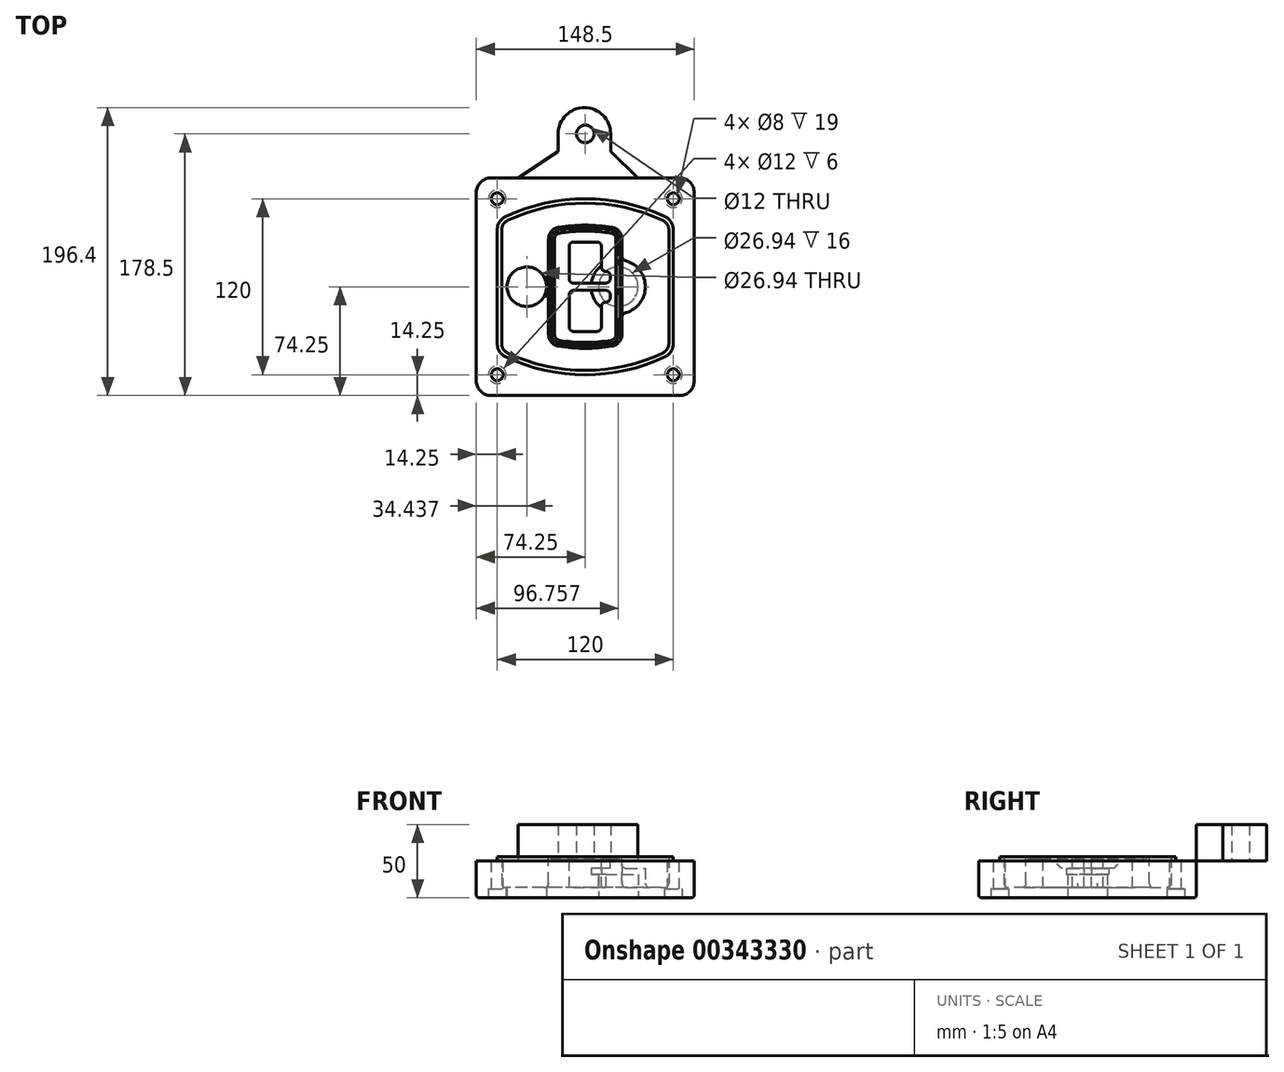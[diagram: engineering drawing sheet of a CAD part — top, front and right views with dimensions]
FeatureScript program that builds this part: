
annotation { "Feature Type Name" : "Feature", "Feature Type Description" : "" }
export const myFeature = defineFeature(function(context is Context, id is Id, definition is map)
    precondition{}
    {
        {
            var Q0;
            Q0=qCreatedBy(makeId("Top.planeOp"),FACE);
            var sketch = newSketch(context, id + "F0", { "sketchPlane" : qUnion([Q0])});
            skPoint(sketch, "E0.rect.middle", {"position": v(0, 0) * mm});
            skLineSegment(sketch, "E1.bottom", {"start": v(-64.25, -74.25) * mm, "end": v(64.25, -74.25) * mm});
            skLineSegment(sketch, "E1.top", {"start": v(-64.25, 74.25) * mm, "end": v(64.25, 74.25) * mm});
            skLineSegment(sketch, "E1.left", {"start": v(-74.25, -64.25) * mm, "end": v(-74.25, 64.25) * mm});
            skLineSegment(sketch, "E1.right", {"start": v(74.25, -64.25) * mm, "end": v(74.25, 64.25) * mm});
            skLineSegment(sketch, "E2", {"start": v(-74.25, 74.25) * mm, "end": v(74.25, -74.25) * mm, "construction": true});
            skLineSegment(sketch, "E3", {"start": v(74.25, 74.25) * mm, "end": v(-74.25, -74.25) * mm, "construction": true});
            skCircle(sketch, "E4", {"center": v(-60, 60) * mm, "radius": 4 * mm});
            skCircle(sketch, "E5", {"center": v(60, 60) * mm, "radius": 4 * mm});
            skCircle(sketch, "E6", {"center": v(60, -60) * mm, "radius": 4 * mm});
            skCircle(sketch, "E7", {"center": v(-60, -60) * mm, "radius": 4 * mm});
            skLineSegment(sketch, "E8", {"start": v(-60, 60) * mm, "end": v(60, 60) * mm, "construction": true});
            skLineSegment(sketch, "E9", {"start": v(60, 60) * mm, "end": v(60, -60) * mm, "construction": true});
            skLineSegment(sketch, "E10", {"start": v(60, -60) * mm, "end": v(-60, -60) * mm, "construction": true});
            skLineSegment(sketch, "E11", {"start": v(-60, -60) * mm, "end": v(-60, 60) * mm, "construction": true});
            skLineSegment(sketch, "E12", {"start": v(-60, 38.83) * mm, "end": v(-60, -38.83) * mm});
            skLineSegment(sketch, "E13", {"start": v(60, 38.83) * mm, "end": v(60, -38.83) * mm});
            skArc(sketch, "E14", {"start": v(54.26, 47.88) * mm, "mid": v(0, 60) * mm, "end": v(-54.26, 47.88) * mm});
            skArc(sketch, "E15", {"start": v(-54.26, -47.88) * mm, "mid": v(0, -60) * mm, "end": v(54.26, -47.88) * mm});
            skLineSegment(sketch, "E16", {"start": v(-60, 0) * mm, "end": v(60, 0) * mm, "construction": true});
            skPoint(sketch, "E17.visualSharp", {"position": v(-60, -45) * mm});
            skArc(sketch, "E17.filletArc", {"start": v(-60, -38.83) * mm, "mid": v(-58.44, -44.2) * mm, "end": v(-54.26, -47.88) * mm});
            skPoint(sketch, "E18.visualSharp", {"position": v(-60, 45) * mm});
            skArc(sketch, "E18.filletArc", {"start": v(-54.26, 47.88) * mm, "mid": v(-58.44, 44.2) * mm, "end": v(-60, 38.83) * mm});
            skPoint(sketch, "E19.visualSharp", {"position": v(60, 45) * mm});
            skArc(sketch, "E19.filletArc", {"start": v(60, 38.83) * mm, "mid": v(58.44, 44.2) * mm, "end": v(54.26, 47.88) * mm});
            skPoint(sketch, "E20.visualSharp", {"position": v(60, -45) * mm});
            skArc(sketch, "E20.filletArc", {"start": v(54.26, -47.88) * mm, "mid": v(58.44, -44.2) * mm, "end": v(60, -38.83) * mm});
            skPoint(sketch, "E21.visualSharp", {"position": v(-74.25, 74.25) * mm});
            skArc(sketch, "E21.filletArc", {"start": v(-64.25, 74.25) * mm, "mid": v(-71.32, 71.32) * mm, "end": v(-74.25, 64.25) * mm});
            skPoint(sketch, "E22.visualSharp", {"position": v(74.25, 74.25) * mm});
            skArc(sketch, "E22.filletArc", {"start": v(74.25, 64.25) * mm, "mid": v(71.32, 71.32) * mm, "end": v(64.25, 74.25) * mm});
            skPoint(sketch, "E23.visualSharp", {"position": v(74.25, -74.25) * mm});
            skArc(sketch, "E23.filletArc", {"start": v(64.25, -74.25) * mm, "mid": v(71.32, -71.32) * mm, "end": v(74.25, -64.25) * mm});
            skPoint(sketch, "E24.visualSharp", {"position": v(-74.25, -74.25) * mm});
            skArc(sketch, "E24.filletArc", {"start": v(-74.25, -64.25) * mm, "mid": v(-71.32, -71.32) * mm, "end": v(-64.25, -74.25) * mm});
            skArc(sketch, "E25.0", {"start": v(57, 38.83) * mm, "mid": v(55.9, 42.58) * mm, "end": v(52.98, 45.17) * mm});
            skLineSegment(sketch, "E25.1", {"start": v(57, 38.83) * mm, "end": v(57, -38.83) * mm});
            skArc(sketch, "E25.2", {"start": v(52.98, -45.17) * mm, "mid": v(55.9, -42.58) * mm, "end": v(57, -38.83) * mm});
            skArc(sketch, "E25.3", {"start": v(-52.98, -45.17) * mm, "mid": v(0, -57) * mm, "end": v(52.98, -45.17) * mm});
            skArc(sketch, "E25.4", {"start": v(-57, -38.83) * mm, "mid": v(-55.9, -42.58) * mm, "end": v(-52.98, -45.17) * mm});
            skArc(sketch, "E25.5", {"start": v(52.98, 45.17) * mm, "mid": v(0, 57) * mm, "end": v(-52.98, 45.17) * mm});
            skLineSegment(sketch, "E25.6", {"start": v(-57, 38.83) * mm, "end": v(-57, -38.83) * mm});
            skArc(sketch, "E25.7", {"start": v(-52.98, 45.17) * mm, "mid": v(-55.9, 42.58) * mm, "end": v(-57, 38.83) * mm});
            skArc(sketch, "E26.0", {"start": v(-55.96, 51.5) * mm, "mid": v(-61.82, 46.33) * mm, "end": v(-64, 38.83) * mm});
            skArc(sketch, "E26.1", {"start": v(55.96, 51.5) * mm, "mid": v(0, 64) * mm, "end": v(-55.96, 51.5) * mm});
            skArc(sketch, "E26.2", {"start": v(64, 38.83) * mm, "mid": v(61.82, 46.33) * mm, "end": v(55.96, 51.5) * mm});
            skLineSegment(sketch, "E26.3", {"start": v(64, 38.83) * mm, "end": v(64, -38.83) * mm});
            skArc(sketch, "E26.4", {"start": v(55.96, -51.5) * mm, "mid": v(61.82, -46.33) * mm, "end": v(64, -38.83) * mm});
            skLineSegment(sketch, "E26.5", {"start": v(-64, 38.83) * mm, "end": v(-64, -38.83) * mm});
            skArc(sketch, "E26.6", {"start": v(-55.96, -51.5) * mm, "mid": v(0, -64) * mm, "end": v(55.96, -51.5) * mm});
            skArc(sketch, "E26.7", {"start": v(-64, -38.83) * mm, "mid": v(-61.82, -46.33) * mm, "end": v(-55.96, -51.5) * mm});
            skSolve(sketch);
        }
        {
            var Q0;
            Q0=makeQuery(id+"F0.imprint","IMPRINT",FACE,{"disambiguationData":[TD([[makeQuery(id+"F0.imprint","IMPRINT",EDGE,{"derivedFrom":sQuery(id+"F0.wireOp",EDGE,"E1.bottom")}),1.0]])]});
            var Q1;
            Q1=makeQuery(id+"F0.imprint","IMPRINT",FACE,{"disambiguationData":[TD([[makeQuery(id+"F0.imprint","IMPRINT",EDGE,{"derivedFrom":sQuery(id+"F0.wireOp",EDGE,"E12")}),1.0]])]});
            var Q2;
            Q2=makeQuery(id+"F0.imprint","IMPRINT",FACE,{"disambiguationData":[TD([[makeQuery(id+"F0.imprint","IMPRINT",EDGE,{"derivedFrom":sQuery(id+"F0.wireOp",EDGE,"E25.0")}),1.0]])]});
            var Q3;
            Q3=makeQuery(id+"F0.imprint","IMPRINT",FACE,{"disambiguationData":[TD([[makeQuery(id+"F0.imprint","IMPRINT",EDGE,{"derivedFrom":sQuery(id+"F0.wireOp",EDGE,"E12")}),-1.0]])]});
            extrude(context, id + "F1", {"entities" : qUnion([Q0, Q1, Q2, Q3]), "oppositeDirection" : true, "depth" : 25 * mm});
        }
        {
            var Q0;
            Q0=makeQuery(id+"F0.imprint","IMPRINT",FACE,{"disambiguationData":[TD([[makeQuery(id+"F0.imprint","IMPRINT",EDGE,{"derivedFrom":sQuery(id+"F0.wireOp",EDGE,"E12")}),1.0]])]});
            extrude(context, id + "F2", {"entities" : qUnion([Q0]), "operationType" : NewBodyOperationType.ADD, "depth" : 3 * mm});
        }
        {
            var Q0;
            Q0=makeQuery(id+"F0.imprint","IMPRINT",FACE,{"disambiguationData":[TD([[makeQuery(id+"F0.imprint","IMPRINT",EDGE,{"derivedFrom":sQuery(id+"F0.wireOp",EDGE,"E25.0")}),1.0]])]});
            extrude(context, id + "F3", {"entities" : qUnion([Q0]), "operationType" : NewBodyOperationType.REMOVE, "oppositeDirection" : true, "depth" : 18 * mm});
        }
        {
            var Q0;
            Q0=makeQuery(id+"F2.opExtrude","CAP_FACE",FACE,{"disambiguationData":[OSD([sQuery(id+"F0.wireOp",EDGE,"E12"),sQuery(id+"F0.wireOp",EDGE,"E13"),sQuery(id+"F0.wireOp",EDGE,"E14"),sQuery(id+"F0.wireOp",EDGE,"E15"),sQuery(id+"F0.wireOp",EDGE,"E17.filletArc"),sQuery(id+"F0.wireOp",EDGE,"E18.filletArc"),sQuery(id+"F0.wireOp",EDGE,"E19.filletArc"),sQuery(id+"F0.wireOp",EDGE,"E20.filletArc"),sQuery(id+"F0.wireOp",EDGE,"E25.0"),sQuery(id+"F0.wireOp",EDGE,"E25.1"),sQuery(id+"F0.wireOp",EDGE,"E25.2"),sQuery(id+"F0.wireOp",EDGE,"E25.3"),sQuery(id+"F0.wireOp",EDGE,"E25.4"),sQuery(id+"F0.wireOp",EDGE,"E25.5"),sQuery(id+"F0.wireOp",EDGE,"E25.6"),sQuery(id+"F0.wireOp",EDGE,"E25.7")])],"isStart":false});
            var sketch = newSketch(context, id + "F4", { "sketchPlane" : qUnion([Q0])});
            skArc(sketch, "E27.0", {"start": v(-18.34, -40.45) * mm, "mid": v(0, -42) * mm, "end": v(18.34, -40.45) * mm});
            skArc(sketch, "E28.0", {"start": v(18.34, 40.45) * mm, "mid": v(0, 42) * mm, "end": v(-18.34, 40.45) * mm});
            skLineSegment(sketch, "E29", {"start": v(-25, 32.57) * mm, "end": v(-25, -32.57) * mm});
            skLineSegment(sketch, "E30", {"start": v(25, 32.57) * mm, "end": v(25, -32.57) * mm});
            skLineSegment(sketch, "E31", {"start": v(-25, 39.1) * mm, "end": v(25, 39.1) * mm, "construction": true});
            skLineSegment(sketch, "E32", {"start": v(-25, -39.1) * mm, "end": v(25, -39.1) * mm, "construction": true});
            skPoint(sketch, "E33.visualSharp", {"position": v(-25, 39.1) * mm});
            skArc(sketch, "E33.filletArc", {"start": v(-18.34, 40.45) * mm, "mid": v(-23.11, 37.73) * mm, "end": v(-25, 32.57) * mm});
            skPoint(sketch, "E34.visualSharp", {"position": v(25, 39.1) * mm});
            skArc(sketch, "E34.filletArc", {"start": v(25, 32.57) * mm, "mid": v(23.11, 37.73) * mm, "end": v(18.34, 40.45) * mm});
            skPoint(sketch, "E35.visualSharp", {"position": v(25, -39.1) * mm});
            skArc(sketch, "E35.filletArc", {"start": v(18.34, -40.45) * mm, "mid": v(23.11, -37.73) * mm, "end": v(25, -32.57) * mm});
            skPoint(sketch, "E36.visualSharp", {"position": v(-25, -39.1) * mm});
            skArc(sketch, "E36.filletArc", {"start": v(-25, -32.57) * mm, "mid": v(-23.11, -37.73) * mm, "end": v(-18.34, -40.45) * mm});
            skArc(sketch, "E37.0", {"start": v(52.98, 45.17) * mm, "mid": v(0, 57) * mm, "end": v(-52.98, 45.17) * mm});
            skArc(sketch, "E37.1", {"start": v(-52.98, 45.17) * mm, "mid": v(-55.9, 42.58) * mm, "end": v(-57, 38.83) * mm});
            skLineSegment(sketch, "E37.2", {"start": v(-57, 38.83) * mm, "end": v(-57, -38.83) * mm});
            skArc(sketch, "E37.3", {"start": v(-57, -38.83) * mm, "mid": v(-55.9, -42.58) * mm, "end": v(-52.98, -45.17) * mm});
            skArc(sketch, "E37.4", {"start": v(-52.98, -45.17) * mm, "mid": v(0, -57) * mm, "end": v(52.98, -45.17) * mm});
            skArc(sketch, "E37.5", {"start": v(52.98, -45.17) * mm, "mid": v(55.9, -42.58) * mm, "end": v(57, -38.83) * mm});
            skLineSegment(sketch, "E37.6", {"start": v(57, 38.83) * mm, "end": v(57, -38.83) * mm});
            skArc(sketch, "E37.7", {"start": v(57, 38.83) * mm, "mid": v(55.9, 42.58) * mm, "end": v(52.98, 45.17) * mm});
            skLineSegment(sketch, "E38.0", {"start": v(23, 32.57) * mm, "end": v(23, -32.57) * mm});
            skArc(sketch, "E38.1", {"start": v(18, -38.48) * mm, "mid": v(21.58, -36.44) * mm, "end": v(23, -32.57) * mm});
            skArc(sketch, "E38.2", {"start": v(-18, -38.48) * mm, "mid": v(0, -40) * mm, "end": v(18, -38.48) * mm});
            skArc(sketch, "E38.3", {"start": v(-23, -32.57) * mm, "mid": v(-21.58, -36.44) * mm, "end": v(-18, -38.48) * mm});
            skLineSegment(sketch, "E38.4", {"start": v(-23, 32.57) * mm, "end": v(-23, -32.57) * mm});
            skArc(sketch, "E38.5", {"start": v(23, 32.57) * mm, "mid": v(21.58, 36.44) * mm, "end": v(18, 38.48) * mm});
            skArc(sketch, "E38.6", {"start": v(-18, 38.48) * mm, "mid": v(-21.58, 36.44) * mm, "end": v(-23, 32.57) * mm});
            skArc(sketch, "E38.7", {"start": v(18, 38.48) * mm, "mid": v(0, 40) * mm, "end": v(-18, 38.48) * mm});
            skArc(sketch, "E39.0", {"start": v(21, 32.57) * mm, "mid": v(20.06, 35.15) * mm, "end": v(17.67, 36.5) * mm});
            skLineSegment(sketch, "E39.1", {"start": v(21, 32.57) * mm, "end": v(21, -32.57) * mm});
            skArc(sketch, "E39.2", {"start": v(17.67, -36.5) * mm, "mid": v(20.06, -35.15) * mm, "end": v(21, -32.57) * mm});
            skArc(sketch, "E39.3", {"start": v(-17.67, -36.5) * mm, "mid": v(0, -38) * mm, "end": v(17.67, -36.5) * mm});
            skArc(sketch, "E39.4", {"start": v(-21, -32.57) * mm, "mid": v(-20.06, -35.15) * mm, "end": v(-17.67, -36.5) * mm});
            skArc(sketch, "E39.5", {"start": v(17.67, 36.5) * mm, "mid": v(0, 38) * mm, "end": v(-17.67, 36.5) * mm});
            skLineSegment(sketch, "E39.6", {"start": v(-21, 32.57) * mm, "end": v(-21, -32.57) * mm});
            skArc(sketch, "E39.7", {"start": v(-17.67, 36.5) * mm, "mid": v(-20.06, 35.15) * mm, "end": v(-21, 32.57) * mm});
            skLineSegment(sketch, "E40", {"start": v(-25, 0) * mm, "end": v(25, 0) * mm, "construction": true});
            skLineSegment(sketch, "E41", {"start": v(-11, 5.5) * mm, "end": v(-11, 27.5) * mm});
            skLineSegment(sketch, "E42", {"start": v(-8, 30.5) * mm, "end": v(8, 30.5) * mm});
            skLineSegment(sketch, "E43", {"start": v(11, 27.5) * mm, "end": v(11, 13.5) * mm});
            skLineSegment(sketch, "E44", {"start": v(14, 10.5) * mm, "end": v(14, 10.5) * mm});
            skLineSegment(sketch, "E45", {"start": v(17, 7.5) * mm, "end": v(17, 5.5) * mm});
            skLineSegment(sketch, "E46", {"start": v(14, 2.5) * mm, "end": v(-8, 2.5) * mm});
            skPoint(sketch, "E47.visualSharp", {"position": v(-11, 30.5) * mm});
            skArc(sketch, "E47.filletArc", {"start": v(-8, 30.5) * mm, "mid": v(-10.12, 29.62) * mm, "end": v(-11, 27.5) * mm});
            skPoint(sketch, "E48.visualSharp", {"position": v(11, 30.5) * mm});
            skArc(sketch, "E48.filletArc", {"start": v(11, 27.5) * mm, "mid": v(10.12, 29.62) * mm, "end": v(8, 30.5) * mm});
            skPoint(sketch, "E49.visualSharp", {"position": v(11, 10.5) * mm});
            skArc(sketch, "E49.filletArc", {"start": v(11, 13.5) * mm, "mid": v(11.88, 11.38) * mm, "end": v(14, 10.5) * mm});
            skPoint(sketch, "E50.visualSharp", {"position": v(17, 10.5) * mm});
            skArc(sketch, "E50.filletArc", {"start": v(17, 7.5) * mm, "mid": v(16.12, 9.62) * mm, "end": v(14, 10.5) * mm});
            skPoint(sketch, "E51.visualSharp", {"position": v(17, 2.5) * mm});
            skArc(sketch, "E51.filletArc", {"start": v(14, 2.5) * mm, "mid": v(16.12, 3.38) * mm, "end": v(17, 5.5) * mm});
            skPoint(sketch, "E52.visualSharp", {"position": v(-11, 2.5) * mm});
            skArc(sketch, "E52.filletArc", {"start": v(-11, 5.5) * mm, "mid": v(-10.12, 3.38) * mm, "end": v(-8, 2.5) * mm});
            skLineSegment(sketch, "E53.0.MirrorCS", {"start": v(14, -2.5) * mm, "end": v(-8, -2.5) * mm});
            skArc(sketch, "E54.0.MirrorCS", {"start": v(-11, -5.5) * mm, "mid": v(-10.12, -3.38) * mm, "end": v(-8, -2.5) * mm});
            skLineSegment(sketch, "E55.0.MirrorCS", {"start": v(-11, -5.5) * mm, "end": v(-11, -27.5) * mm});
            skArc(sketch, "E56.0.MirrorCS", {"start": v(-8, -30.5) * mm, "mid": v(-10.12, -29.62) * mm, "end": v(-11, -27.5) * mm});
            skLineSegment(sketch, "E57.0.MirrorCS", {"start": v(-8, -30.5) * mm, "end": v(8, -30.5) * mm});
            skArc(sketch, "E58.0.MirrorCS", {"start": v(11, -27.5) * mm, "mid": v(10.12, -29.62) * mm, "end": v(8, -30.5) * mm});
            skLineSegment(sketch, "E59.0.MirrorCS", {"start": v(11, -27.5) * mm, "end": v(11, -13.5) * mm});
            skArc(sketch, "E60.0.MirrorCS", {"start": v(11, -13.5) * mm, "mid": v(11.88, -11.38) * mm, "end": v(14, -10.5) * mm});
            skArc(sketch, "E61.0.MirrorCS", {"start": v(17, -7.5) * mm, "mid": v(16.12, -9.62) * mm, "end": v(14, -10.5) * mm});
            skLineSegment(sketch, "E62.0.MirrorCS", {"start": v(17, -7.5) * mm, "end": v(17, -5.5) * mm});
            skArc(sketch, "E63.0.MirrorCS", {"start": v(14, -2.5) * mm, "mid": v(16.12, -3.38) * mm, "end": v(17, -5.5) * mm});
            skSolve(sketch);
        }
        {
            var Q0;
            Q0=makeQuery(id+"F4.imprint","IMPRINT",FACE,{"disambiguationData":[TD([[makeQuery(id+"F4.imprint","IMPRINT",EDGE,{"derivedFrom":sQuery(id+"F4.wireOp",EDGE,"E27.0")}),1.0]])]});
            var Q1;
            Q1=makeQuery(id+"F4.imprint","IMPRINT",FACE,{"disambiguationData":[TD([[makeQuery(id+"F4.imprint","IMPRINT",EDGE,{"derivedFrom":sQuery(id+"F4.wireOp",EDGE,"E38.0")}),-1.0]])]});
            var Q2;
            Q2=makeQuery(id+"F4.imprint","IMPRINT",FACE,{"disambiguationData":[TD([[makeQuery(id+"F4.imprint","IMPRINT",EDGE,{"derivedFrom":sQuery(id+"F4.wireOp",EDGE,"E39.0")}),1.0]])]});
            extrude(context, id + "F5", {"entities" : qUnion([Q0, Q1, Q2]), "operationType" : NewBodyOperationType.ADD, "endBound" : BoundingType.UP_TO_NEXT, "oppositeDirection" : true, "depth" : 25 * mm});
        }
        {
            var Q0;
            Q0=makeQuery(id+"F4.imprint","IMPRINT",FACE,{"disambiguationData":[TD([[makeQuery(id+"F4.imprint","IMPRINT",EDGE,{"derivedFrom":sQuery(id+"F4.wireOp",EDGE,"E38.0")}),-1.0]])]});
            extrude(context, id + "F6", {"entities" : qUnion([Q0]), "operationType" : NewBodyOperationType.REMOVE, "oppositeDirection" : true, "depth" : 2 * mm});
        }
        {
            var Q0;
            Q0=makeQuery(id+"F1.opExtrude","CAP_FACE",FACE,{"disambiguationData":[OSD([sQuery(id+"F0.wireOp",EDGE,"E1.bottom"),sQuery(id+"F0.wireOp",EDGE,"E1.top"),sQuery(id+"F0.wireOp",EDGE,"E1.left"),sQuery(id+"F0.wireOp",EDGE,"E1.right"),sQuery(id+"F0.wireOp",EDGE,"E4"),sQuery(id+"F0.wireOp",EDGE,"E5"),sQuery(id+"F0.wireOp",EDGE,"E6"),sQuery(id+"F0.wireOp",EDGE,"E7"),sQuery(id+"F0.wireOp",EDGE,"E21.filletArc"),sQuery(id+"F0.wireOp",EDGE,"E22.filletArc"),sQuery(id+"F0.wireOp",EDGE,"E23.filletArc"),sQuery(id+"F0.wireOp",EDGE,"E24.filletArc")])],"isStart":false});
            var sketch = newSketch(context, id + "F7", { "sketchPlane" : qUnion([Q0])});
            skCircle(sketch, "E64", {"center": v(22.5, 0) * mm, "radius": 13.47 * mm});
            skCircle(sketch, "E65", {"center": v(-39.81, 0) * mm, "radius": 13.47 * mm});
            skLineSegment(sketch, "E66", {"start": v(74.25, 0) * mm, "end": v(-74.25, 0) * mm});
            skCircle(sketch, "E67", {"center": v(22.5, 0) * mm, "radius": 18.47 * mm});
            skCircle(sketch, "E68", {"center": v(60, -60) * mm, "radius": 6 * mm});
            skCircle(sketch, "E69", {"center": v(-60, -60) * mm, "radius": 6 * mm});
            skCircle(sketch, "E70", {"center": v(-60, 60) * mm, "radius": 6 * mm});
            skCircle(sketch, "E71", {"center": v(60, 60) * mm, "radius": 6 * mm});
            skSolve(sketch);
        }
        {
            var Q0;
            {var subQ1=sQuery(id+"F7.wireOp",EDGE,"E66");var subQ4=sQuery(id+"F7.wireOp",EDGE,"E64");var subQ6=makeQuery(id+"F7.imprint","INTERSECT",VERTEX,{"disambiguationData":[OD(0.0)],"derivedFrom":[subQ4,subQ1]});Q0=makeQuery(id+"F7.imprint","IMPRINT",FACE,{"disambiguationData":[TD([[makeQuery(id+"F7.imprint","IMPRINT",EDGE,{"disambiguationData":[TD([[subQ6,-1.0]])],"derivedFrom":subQ4}),-1.0]])]});}
            var Q1;
            {var subQ0=sQuery(id+"F7.wireOp",EDGE,"E66");var subQ1=sQuery(id+"F7.wireOp",EDGE,"E64");var subQ3=makeQuery(id+"F7.imprint","INTERSECT",VERTEX,{"disambiguationData":[OD(0.0)],"derivedFrom":[subQ1,subQ0]});Q1=makeQuery(id+"F7.imprint","IMPRINT",FACE,{"disambiguationData":[TD([[makeQuery(id+"F7.imprint","IMPRINT",EDGE,{"disambiguationData":[TD([[subQ3,-1.0]])],"derivedFrom":subQ1}),1.0]])]});}
            var Q2;
            {var subQ0=sQuery(id+"F7.wireOp",EDGE,"E66");var subQ1=sQuery(id+"F7.wireOp",EDGE,"E64");var subQ3=makeQuery(id+"F7.imprint","INTERSECT",VERTEX,{"disambiguationData":[OD(0.0)],"derivedFrom":[subQ1,subQ0]});Q2=makeQuery(id+"F7.imprint","IMPRINT",FACE,{"disambiguationData":[TD([[makeQuery(id+"F7.imprint","IMPRINT",EDGE,{"disambiguationData":[TD([[subQ3,1.0]])],"derivedFrom":subQ1}),1.0]])]});}
            var Q3;
            {var subQ1=sQuery(id+"F7.wireOp",EDGE,"E66");var subQ4=sQuery(id+"F7.wireOp",EDGE,"E64");var subQ6=makeQuery(id+"F7.imprint","INTERSECT",VERTEX,{"disambiguationData":[OD(0.0)],"derivedFrom":[subQ4,subQ1]});Q3=makeQuery(id+"F7.imprint","IMPRINT",FACE,{"disambiguationData":[TD([[makeQuery(id+"F7.imprint","IMPRINT",EDGE,{"disambiguationData":[TD([[subQ6,1.0]])],"derivedFrom":subQ4}),-1.0]])]});}
            extrude(context, id + "F8", {"entities" : qUnion([Q0, Q1, Q2, Q3]), "operationType" : NewBodyOperationType.ADD, "oppositeDirection" : true, "depth" : 20 * mm});
        }
        {
            var Q0;
            {var subQ0=sQuery(id+"F7.wireOp",EDGE,"E66");var subQ1=sQuery(id+"F7.wireOp",EDGE,"E64");var subQ3=makeQuery(id+"F7.imprint","INTERSECT",VERTEX,{"disambiguationData":[OD(0.0)],"derivedFrom":[subQ1,subQ0]});Q0=makeQuery(id+"F7.imprint","IMPRINT",FACE,{"disambiguationData":[TD([[makeQuery(id+"F7.imprint","IMPRINT",EDGE,{"disambiguationData":[TD([[subQ3,-1.0]])],"derivedFrom":subQ1}),1.0]])]});}
            var Q1;
            {var subQ0=sQuery(id+"F7.wireOp",EDGE,"E66");var subQ1=sQuery(id+"F7.wireOp",EDGE,"E64");var subQ3=makeQuery(id+"F7.imprint","INTERSECT",VERTEX,{"disambiguationData":[OD(0.0)],"derivedFrom":[subQ1,subQ0]});Q1=makeQuery(id+"F7.imprint","IMPRINT",FACE,{"disambiguationData":[TD([[makeQuery(id+"F7.imprint","IMPRINT",EDGE,{"disambiguationData":[TD([[subQ3,1.0]])],"derivedFrom":subQ1}),1.0]])]});}
            extrude(context, id + "F9", {"entities" : qUnion([Q0, Q1]), "operationType" : NewBodyOperationType.REMOVE, "oppositeDirection" : true, "depth" : 16 * mm});
        }
        {
            var Q0;
            {var subQ0=sQuery(id+"F7.wireOp",EDGE,"E66");var subQ1=sQuery(id+"F7.wireOp",EDGE,"E65");var subQ3=makeQuery(id+"F7.imprint","INTERSECT",VERTEX,{"disambiguationData":[OD(0.0)],"derivedFrom":[subQ1,subQ0]});Q0=makeQuery(id+"F7.imprint","IMPRINT",FACE,{"disambiguationData":[TD([[makeQuery(id+"F7.imprint","IMPRINT",EDGE,{"disambiguationData":[TD([[subQ3,-1.0]])],"derivedFrom":subQ1}),1.0]])]});}
            var Q1;
            {var subQ0=sQuery(id+"F7.wireOp",EDGE,"E66");var subQ1=sQuery(id+"F7.wireOp",EDGE,"E65");var subQ3=makeQuery(id+"F7.imprint","INTERSECT",VERTEX,{"disambiguationData":[OD(0.0)],"derivedFrom":[subQ1,subQ0]});Q1=makeQuery(id+"F7.imprint","IMPRINT",FACE,{"disambiguationData":[TD([[makeQuery(id+"F7.imprint","IMPRINT",EDGE,{"disambiguationData":[TD([[subQ3,1.0]])],"derivedFrom":subQ1}),1.0]])]});}
            extrude(context, id + "F10", {"entities" : qUnion([Q0, Q1]), "operationType" : NewBodyOperationType.REMOVE, "oppositeDirection" : true, "depth" : 25 * mm});
        }
        {
            var Q0;
            Q0=makeQuery(id+"F7.imprint","IMPRINT",FACE,{"disambiguationData":[TD([[makeQuery(id+"F7.imprint","IMPRINT",EDGE,{"derivedFrom":sQuery(id+"F7.wireOp",EDGE,"E68")}),1.0]])]});
            var Q1;
            Q1=makeQuery(id+"F7.imprint","IMPRINT",FACE,{"disambiguationData":[TD([[makeQuery(id+"F7.imprint","IMPRINT",EDGE,{"derivedFrom":makeQuery(id+"F1.opExtrude","CAP_EDGE",EDGE,{"disambiguationData":[OSD([sQuery(id+"F0.wireOp",EDGE,"E5")])],"isStart":false})}),-1.0]])]});
            var Q2;
            Q2=makeQuery(id+"F7.imprint","IMPRINT",FACE,{"disambiguationData":[TD([[makeQuery(id+"F7.imprint","IMPRINT",EDGE,{"derivedFrom":sQuery(id+"F7.wireOp",EDGE,"E69")}),1.0]])]});
            var Q3;
            Q3=makeQuery(id+"F7.imprint","IMPRINT",FACE,{"disambiguationData":[TD([[makeQuery(id+"F7.imprint","IMPRINT",EDGE,{"derivedFrom":makeQuery(id+"F1.opExtrude","CAP_EDGE",EDGE,{"disambiguationData":[OSD([sQuery(id+"F0.wireOp",EDGE,"E4")])],"isStart":false})}),-1.0]])]});
            var Q4;
            Q4=makeQuery(id+"F7.imprint","IMPRINT",FACE,{"disambiguationData":[TD([[makeQuery(id+"F7.imprint","IMPRINT",EDGE,{"derivedFrom":sQuery(id+"F7.wireOp",EDGE,"E70")}),1.0]])]});
            var Q5;
            Q5=makeQuery(id+"F7.imprint","IMPRINT",FACE,{"disambiguationData":[TD([[makeQuery(id+"F7.imprint","IMPRINT",EDGE,{"derivedFrom":makeQuery(id+"F1.opExtrude","CAP_EDGE",EDGE,{"disambiguationData":[OSD([sQuery(id+"F0.wireOp",EDGE,"E7")])],"isStart":false})}),-1.0]])]});
            var Q6;
            Q6=makeQuery(id+"F7.imprint","IMPRINT",FACE,{"disambiguationData":[TD([[makeQuery(id+"F7.imprint","IMPRINT",EDGE,{"derivedFrom":sQuery(id+"F7.wireOp",EDGE,"E71")}),1.0]])]});
            var Q7;
            Q7=makeQuery(id+"F7.imprint","IMPRINT",FACE,{"disambiguationData":[TD([[makeQuery(id+"F7.imprint","IMPRINT",EDGE,{"derivedFrom":makeQuery(id+"F1.opExtrude","CAP_EDGE",EDGE,{"disambiguationData":[OSD([sQuery(id+"F0.wireOp",EDGE,"E6")])],"isStart":false})}),-1.0]])]});
            extrude(context, id + "F11", {"entities" : qUnion([Q0, Q1, Q2, Q3, Q4, Q5, Q6, Q7]), "operationType" : NewBodyOperationType.REMOVE, "oppositeDirection" : true, "depth" : 6 * mm});
        }
        {
            var Q0;
            Q0=makeQuery(id+"F9.boolean.opBoolean","COPY",FACE,{"derivedFrom":makeQuery(id+"F9.opExtrude","CAP_FACE",FACE,{"disambiguationData":[OSD([sQuery(id+"F7.wireOp",EDGE,"E64")])],"isStart":false})});
            var sketch = newSketch(context, id + "F12", { "sketchPlane" : qUnion([Q0])});
            skArc(sketch, "E72.0", {"start": v(11, 14.45) * mm, "mid": v(6.45, 9.13) * mm, "end": v(4.2, 2.5) * mm});
            skArc(sketch, "E72.1", {"start": v(4.2, -2.5) * mm, "mid": v(6.45, -9.13) * mm, "end": v(11, -14.45) * mm});
            skLineSegment(sketch, "E73", {"start": v(4.2, -2.5) * mm, "end": v(14, -2.5) * mm});
            skLineSegment(sketch, "E74.0", {"start": v(14, 2.5) * mm, "end": v(4.2, 2.5) * mm});
            skArc(sketch, "E74.1", {"start": v(14, 2.5) * mm, "mid": v(16.12, 3.38) * mm, "end": v(17, 5.5) * mm});
            skLineSegment(sketch, "E74.2", {"start": v(17, 7.5) * mm, "end": v(17, 5.5) * mm});
            skArc(sketch, "E74.3", {"start": v(17, 7.5) * mm, "mid": v(16.12, 9.62) * mm, "end": v(14, 10.5) * mm});
            skArc(sketch, "E74.4", {"start": v(11, 13.5) * mm, "mid": v(11.88, 11.38) * mm, "end": v(14, 10.5) * mm});
            skLineSegment(sketch, "E74.5", {"start": v(11, 14.45) * mm, "end": v(11, 13.5) * mm});
            skLineSegment(sketch, "E74.7", {"start": v(14, -2.5) * mm, "end": v(4.2, -2.5) * mm});
            skArc(sketch, "E74.8", {"start": v(14, -2.5) * mm, "mid": v(16.12, -3.38) * mm, "end": v(17, -5.5) * mm});
            skLineSegment(sketch, "E74.9", {"start": v(17, -7.5) * mm, "end": v(17, -5.5) * mm});
            skArc(sketch, "E74.10", {"start": v(17, -7.5) * mm, "mid": v(16.12, -9.62) * mm, "end": v(14, -10.5) * mm});
            skArc(sketch, "E74.11", {"start": v(11, -13.5) * mm, "mid": v(11.88, -11.38) * mm, "end": v(14, -10.5) * mm});
            skLineSegment(sketch, "E74.12", {"start": v(11, -14.45) * mm, "end": v(11, -13.5) * mm});
            skPoint(sketch, "E75.orphan", {"position": v(11, -27.5) * mm});
            skPoint(sketch, "E76.orphan", {"position": v(-8, -2.5) * mm});
            skPoint(sketch, "E77.orphan", {"position": v(-8, 2.5) * mm});
            skPoint(sketch, "E78.orphan", {"position": v(11, 27.5) * mm});
            skSolve(sketch);
        }
        {
            var Q0;
            {var subQ7=sQuery(id+"F12.wireOp",EDGE,"E72.0");var subQ14=sQuery(id+"F12.wireOp",EDGE,"E72.1");var subQ16=sQuery(id+"F12.wireOp",EDGE,"E74.1");var subQ18=sQuery(id+"F12.wireOp",EDGE,"E74.8");Q0=qUnion([makeQuery(id+"F12.imprint","IMPRINT",FACE,{"disambiguationData":[TD([[makeQuery(id+"F12.imprint","IMPRINT",EDGE,{"derivedFrom":subQ7}),1.0]])]}),makeQuery(id+"F12.imprint","IMPRINT",FACE,{"disambiguationData":[TD([[makeQuery(id+"F12.imprint","IMPRINT",EDGE,{"derivedFrom":subQ14}),1.0]])]}),makeQuery(id+"F12.imprint","IMPRINT",FACE,{"disambiguationData":[TD([[makeQuery(id+"F12.imprint","IMPRINT",EDGE,{"derivedFrom":subQ16}),1.0]])]}),makeQuery(id+"F12.imprint","IMPRINT",FACE,{"disambiguationData":[TD([[makeQuery(id+"F12.imprint","IMPRINT",EDGE,{"derivedFrom":subQ18}),-1.0]])]})]);}
            var Q1;
            Q1=makeQuery(id+"F5.boolean.opBoolean","SPLIT",FACE,{"disambiguationData":[TD([makeQuery(id+"F5.opExtrude","SWEPT_FACE",FACE,{"disambiguationData":[OSD([sQuery(id+"F4.wireOp",EDGE,"E41")])]})])],"derivedFrom":makeQuery(id+"F3.boolean.opBoolean","COPY",FACE,{"derivedFrom":makeQuery(id+"F3.opExtrude","CAP_FACE",FACE,{"disambiguationData":[OSD([sQuery(id+"F0.wireOp",EDGE,"E25.0"),sQuery(id+"F0.wireOp",EDGE,"E25.1"),sQuery(id+"F0.wireOp",EDGE,"E25.2"),sQuery(id+"F0.wireOp",EDGE,"E25.3"),sQuery(id+"F0.wireOp",EDGE,"E25.4"),sQuery(id+"F0.wireOp",EDGE,"E25.5"),sQuery(id+"F0.wireOp",EDGE,"E25.6"),sQuery(id+"F0.wireOp",EDGE,"E25.7")])],"isStart":false})})});
            extrude(context, id + "F13", {"entities" : qUnion([Q0]), "operationType" : NewBodyOperationType.REMOVE, "endBound" : BoundingType.UP_TO_SURFACE, "endBoundEntityFace" : qUnion([Q1]), "depth" : 25 * mm});
        }
        {
            var Q0;
            Q0=makeQuery(id+"F3.boolean.opBoolean","COPY",EDGE,{"derivedFrom":makeQuery(id+"F3.opExtrude","CAP_EDGE",EDGE,{"disambiguationData":[OSD([sQuery(id+"F0.wireOp",EDGE,"E25.6")])],"isStart":false})});
            var Q1;
            Q1=makeQuery(id+"F8.boolean.opBoolean","INTERSECT",EDGE,{"derivedFrom":[makeQuery(id+"F5.opExtrude","SWEPT_FACE",FACE,{"disambiguationData":[OSD([sQuery(id+"F4.wireOp",EDGE,"E30")])]}),makeQuery(id+"F8.opExtrude","CAP_FACE",FACE,{"disambiguationData":[OSD([sQuery(id+"F7.wireOp",EDGE,"E67")])],"isStart":false})]});
            var Q2;
            Q2=makeQuery(id+"F8.boolean.opBoolean","INTERSECT",EDGE,{"disambiguationData":[OD(1.0)],"derivedFrom":[makeQuery(id+"F5.opExtrude","SWEPT_FACE",FACE,{"disambiguationData":[OSD([sQuery(id+"F4.wireOp",EDGE,"E30")])]}),makeQuery(id+"F8.opExtrude","SWEPT_FACE",FACE,{"disambiguationData":[OSD([sQuery(id+"F7.wireOp",EDGE,"E67")])]})]});
            var Q3;
            {var subQ0=sQuery(id+"F4.wireOp",EDGE,"E30");Q3=makeQuery(id+"F8.boolean.opBoolean","SPLIT",EDGE,{"disambiguationData":[TD([makeQuery(id+"F5.opExtrude","SWEPT_FACE",FACE,{"disambiguationData":[OSD([sQuery(id+"F4.wireOp",EDGE,"E35.filletArc")])]})])],"derivedFrom":makeQuery(id+"F5.opExtrude","CAP_EDGE",EDGE,{"disambiguationData":[OSD([subQ0])],"isStart":false})});}
            var Q4;
            {var subQ0=sQuery(id+"F0.wireOp",EDGE,"E25.7");var subQ1=sQuery(id+"F0.wireOp",EDGE,"E25.1");var subQ2=sQuery(id+"F0.wireOp",EDGE,"E25.6");var subQ3=sQuery(id+"F0.wireOp",EDGE,"E25.5");var subQ4=sQuery(id+"F0.wireOp",EDGE,"E25.4");var subQ5=sQuery(id+"F0.wireOp",EDGE,"E25.0");var subQ6=sQuery(id+"F0.wireOp",EDGE,"E25.2");var subQ7=sQuery(id+"F0.wireOp",EDGE,"E25.3");Q4=makeQuery(id+"F8.boolean.opBoolean","INTERSECT",EDGE,{"derivedFrom":[makeQuery(id+"F5.boolean.opBoolean","SPLIT",FACE,{"disambiguationData":[TD([makeQuery(id+"F2.opExtrude","SWEPT_FACE",FACE,{"disambiguationData":[OSD([subQ5])]})])],"derivedFrom":makeQuery(id+"F3.boolean.opBoolean","COPY",FACE,{"derivedFrom":makeQuery(id+"F3.opExtrude","CAP_FACE",FACE,{"disambiguationData":[OSD([subQ5,subQ1,subQ6,subQ7,subQ4,subQ3,subQ2,subQ0])],"isStart":false})})}),makeQuery(id+"F8.opExtrude","SWEPT_FACE",FACE,{"disambiguationData":[OSD([sQuery(id+"F7.wireOp",EDGE,"E67")])]})]});}
            var Q5;
            Q5=makeQuery(id+"F8.boolean.opBoolean","INTERSECT",EDGE,{"disambiguationData":[OD(0.0)],"derivedFrom":[makeQuery(id+"F5.opExtrude","SWEPT_FACE",FACE,{"disambiguationData":[OSD([sQuery(id+"F4.wireOp",EDGE,"E30")])]}),makeQuery(id+"F8.opExtrude","SWEPT_FACE",FACE,{"disambiguationData":[OSD([sQuery(id+"F7.wireOp",EDGE,"E67")])]})]});
            fillet(context, id + "F14", {"entities" : qUnion([Q0, Q1, Q2, Q3, Q4, Q5]), "radius" : 3 * mm, "tangentPropagation" : true, "allowEdgeOverflow" : false});
        }
        {
            var Q0;
            Q0=makeQuery(id+"F1.opExtrude","CAP_EDGE",EDGE,{"disambiguationData":[OSD([sQuery(id+"F0.wireOp",EDGE,"E1.bottom")])],"isStart":false});
            fillet(context, id + "F15", {"entities" : qUnion([Q0]), "radius" : 2 * mm, "tangentPropagation" : true, "allowEdgeOverflow" : false});
        }
        {
            var Q0;
            {var subQ0=sQuery(id+"F0.wireOp",EDGE,"E21.filletArc");var subQ1=sQuery(id+"F0.wireOp",EDGE,"E7");var subQ2=sQuery(id+"F0.wireOp",EDGE,"E6");var subQ3=sQuery(id+"F0.wireOp",EDGE,"E5");var subQ4=sQuery(id+"F0.wireOp",EDGE,"E4");var subQ5=sQuery(id+"F0.wireOp",EDGE,"E22.filletArc");var subQ6=sQuery(id+"F0.wireOp",EDGE,"E1.bottom");var subQ7=sQuery(id+"F0.wireOp",EDGE,"E1.right");var subQ8=sQuery(id+"F0.wireOp",EDGE,"E1.top");var subQ9=sQuery(id+"F0.wireOp",EDGE,"E1.left");var subQ10=sQuery(id+"F0.wireOp",EDGE,"E23.filletArc");var subQ11=sQuery(id+"F0.wireOp",EDGE,"E24.filletArc");Q0=makeQuery(id+"F2.boolean.opBoolean","SPLIT",FACE,{"disambiguationData":[TD([makeQuery(id+"F1.opExtrude","SWEPT_FACE",FACE,{"disambiguationData":[OSD([subQ6])]})])],"derivedFrom":makeQuery(id+"F1.opExtrude","CAP_FACE",FACE,{"disambiguationData":[OSD([subQ6,subQ8,subQ9,subQ7,subQ4,subQ3,subQ2,subQ1,subQ0,subQ5,subQ10,subQ11])],"isStart":true})});}
            var sketch = newSketch(context, id + "F16", { "sketchPlane" : qUnion([Q0])});
            skLineSegment(sketch, "E79", {"start": v(0, 74.25) * mm, "end": v(0, 104.25) * mm, "construction": true});
            skCircle(sketch, "E80", {"center": v(0, 104.25) * mm, "radius": 6 * mm});
            skLineSegment(sketch, "E81", {"start": v(-45.76, 74.25) * mm, "end": v(-18.45, 92.25) * mm});
            skLineSegment(sketch, "E82", {"start": v(-18.45, 92.25) * mm, "end": v(-18.45, 104.25) * mm});
            skLineSegment(sketch, "E83", {"start": v(35.8, 74.25) * mm, "end": v(17.34, 92.25) * mm});
            skLineSegment(sketch, "E84", {"start": v(17.34, 92.25) * mm, "end": v(17.34, 104.25) * mm});
            skArc(sketch, "E85", {"start": v(17.34, 104.25) * mm, "mid": v(-0.55, 122.15) * mm, "end": v(-18.45, 104.25) * mm});
            skSolve(sketch);
        }
        {
            var Q0;
            Q0=makeQuery(id+"F16.imprint","IMPRINT",FACE,{"disambiguationData":[TD([[makeQuery(id+"F16.imprint","IMPRINT",EDGE,{"derivedFrom":sQuery(id+"F16.wireOp",EDGE,"E80")}),-1.0]])]});
            extrude(context, id + "F17", {"entities" : qUnion([Q0]), "depth" : 25 * mm});
        }
    });
